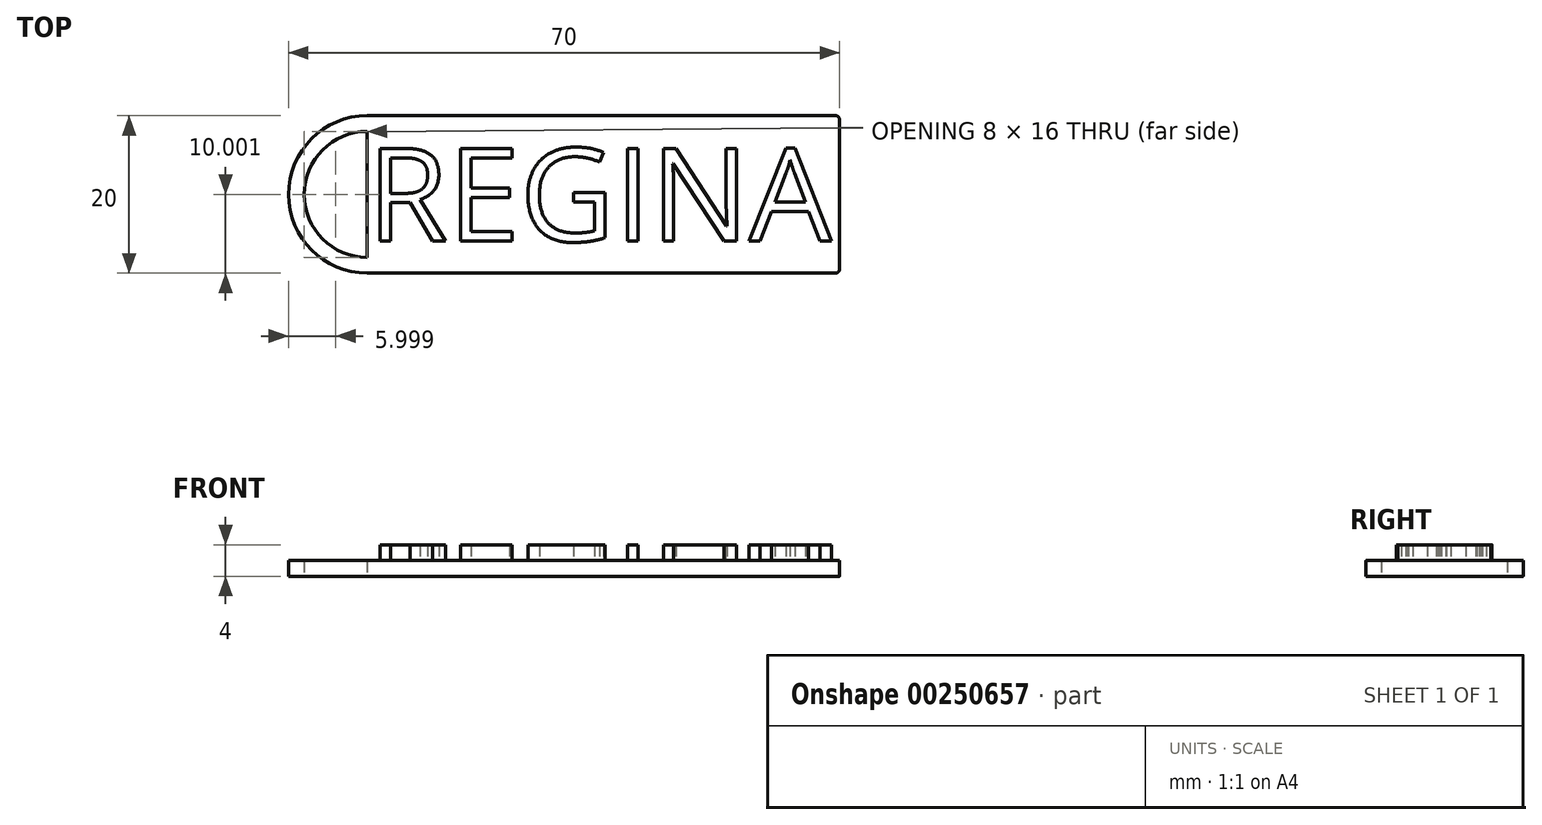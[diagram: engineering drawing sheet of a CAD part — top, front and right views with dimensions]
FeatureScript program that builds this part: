
annotation { "Feature Type Name" : "Feature", "Feature Type Description" : "" }
export const myFeature = defineFeature(function(context is Context, id is Id, definition is map)
    precondition{}
    {
        {
            var Q0;
            Q0=qCreatedBy(makeId("Top.planeOp"),FACE);
            var sketch = newSketch(context, id + "F0", { "sketchPlane" : qUnion([Q0]), "disableImprinting" : false});
            skLineSegment(sketch, "E0.bottom", {"start": v(-5.27, 3.22) * mm, "end": v(54.73, 3.22) * mm});
            skLineSegment(sketch, "E0.top", {"start": v(-5.27, -16.78) * mm, "end": v(54.73, -16.78) * mm});
            skLineSegment(sketch, "E0.left", {"start": v(-5.27, 3.22) * mm, "end": v(-5.27, -16.78) * mm});
            skLineSegment(sketch, "E0.right", {"start": v(54.73, 3.22) * mm, "end": v(54.73, -16.78) * mm});
            skArc(sketch, "E1", {"start": v(-5.27, 3.22) * mm, "mid": v(-15.27, -6.78) * mm, "end": v(-5.27, -16.78) * mm});
            skArc(sketch, "E2", {"start": v(-5.27, 1.22) * mm, "mid": v(-13.27, -6.78) * mm, "end": v(-5.27, -14.78) * mm});
            skSolve(sketch);
        }
        {
            var Q0;
            Q0=qSketchRegion(id+"F0",true);
            extrude(context, id + "F4", {"entities" : qUnion([Q0]), "depth" : 2 * mm});
        }
        {
            var Q0;
            Q0=makeQuery(id+"F4.opExtrude","CAP_FACE",FACE,{"disambiguationData":[OSD([sQuery(id+"F0.wireOp",EDGE,"E0.bottom"),sQuery(id+"F0.wireOp",EDGE,"E0.top"),sQuery(id+"F0.wireOp",EDGE,"E0.left"),sQuery(id+"F0.wireOp",EDGE,"E0.right")])],"isStart":false});
            var sketch = newSketch(context, id + "F1", { "sketchPlane" : qUnion([Q0]), "disableImprinting" : false});
            skText(sketch, "E3", { "text": "REGINA", "fontName": "OpenSans-Regular.ttf"});
            skPoint(sketch, "E4", {"position": v(24.73, -6.78) * mm});
            skLineSegment(sketch, "E5", {"start": v(24.73, 3.22) * mm, "end": v(24.73, -16.78) * mm, "construction": true});
            const initialGuessF1  = {"E3": [-0.00527, -0.01273, 1, 0, 0.0119]};
            skSetInitialGuess(sketch, initialGuessF1);
            skSolve(sketch);
        }
        {
            var Q0;
            Q0=qSketchRegion(id+"F1",true);
            extrude(context, id + "F2", {"entities" : qUnion([Q0]), "operationType" : NewBodyOperationType.ADD, "flatOperationType" : FlatOperationType.REMOVE, "offsetDistance" : 25 * mm, "depth" : 2 * mm, "domain" : OperationDomain.MODEL});
        }
        {
            var Q0;
            Q0=makeQuery(id+"F4.opExtrude","SWEPT_EDGE",EDGE,{"disambiguationData":[OSD([sQuery(id+"F0.wireOp",EDGE,"E0.top"),sQuery(id+"F0.wireOp",EDGE,"E0.right")])]});
            var Q1;
            Q1=makeQuery(id+"F4.opExtrude","SWEPT_EDGE",EDGE,{"disambiguationData":[OSD([sQuery(id+"F0.wireOp",EDGE,"E0.bottom"),sQuery(id+"F0.wireOp",EDGE,"E0.right")])]});
            fillet(context, id + "F3", {"entities" : qUnion([Q0, Q1]), "radius" : 0.5 * mm, "tangentPropagation" : true, "allowEdgeOverflow" : false});
        }
    });
